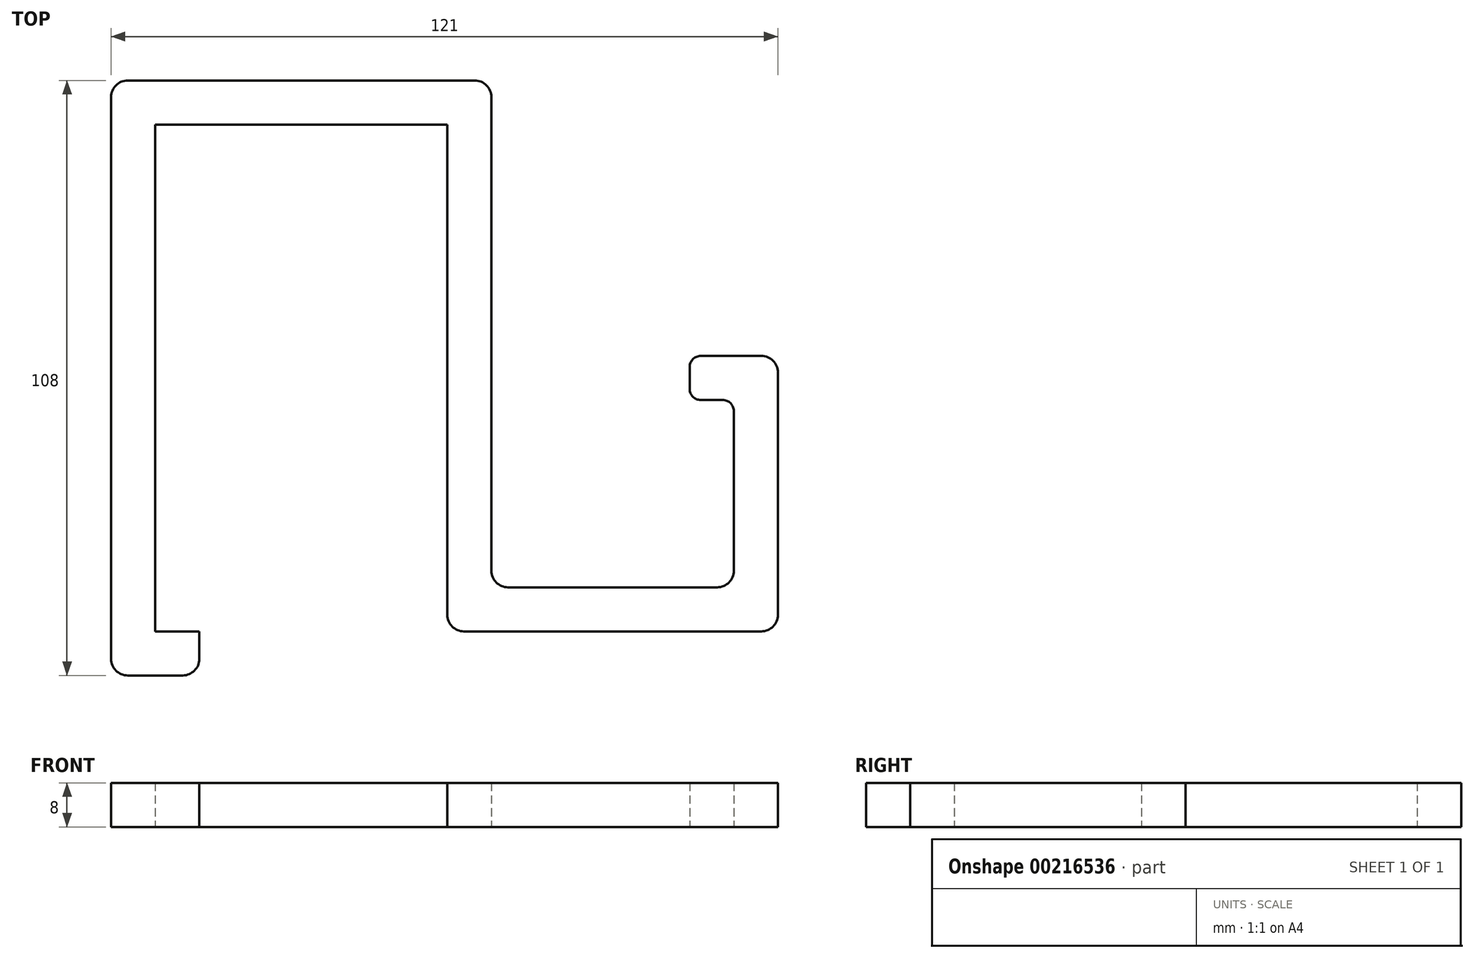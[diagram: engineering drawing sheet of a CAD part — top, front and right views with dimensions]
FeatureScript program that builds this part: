
annotation { "Feature Type Name" : "Feature", "Feature Type Description" : "" }
export const myFeature = defineFeature(function(context is Context, id is Id, definition is map)
    precondition{}
    {
        {
            assignVariable(context, id + "F0", {"name" : "dik", "anyValue" : 8});
        }
        {
            var Q0;
            Q0=qCreatedBy(makeId("Top.planeOp"),FACE);
            var sketch = newSketch(context, id + "F1", { "sketchPlane" : qUnion([Q0])});
            skLineSegment(sketch, "E0", {"start": v(0, 0) * mm, "end": v(0, 92) * mm});
            skLineSegment(sketch, "E1", {"start": v(0, 92) * mm, "end": v(53, 92) * mm});
            skLineSegment(sketch, "E2", {"start": v(53, 92) * mm, "end": v(53, 3) * mm});
            skLineSegment(sketch, "E3", {"start": v(0, 0) * mm, "end": v(-8, 0) * mm, "construction": true});
            skLineSegment(sketch, "E4", {"start": v(-8, 0) * mm, "end": v(-8, 97) * mm});
            skLineSegment(sketch, "E5", {"start": v(-5, 100) * mm, "end": v(58, 100) * mm});
            skLineSegment(sketch, "E6", {"start": v(61, 97) * mm, "end": v(61, 11) * mm});
            skLineSegment(sketch, "E7", {"start": v(56, 0) * mm, "end": v(110, 0) * mm});
            skLineSegment(sketch, "E8", {"start": v(113, 3) * mm, "end": v(113, 47) * mm});
            skLineSegment(sketch, "E9", {"start": v(110, 50) * mm, "end": v(105, 50) * mm});
            skLineSegment(sketch, "E10", {"start": v(105, 40) * mm, "end": v(105, 11) * mm});
            skLineSegment(sketch, "E11", {"start": v(102, 8) * mm, "end": v(64, 8) * mm});
            skLineSegment(sketch, "E12", {"start": v(105, 50) * mm, "end": v(99, 50) * mm});
            skLineSegment(sketch, "E13", {"start": v(97, 48) * mm, "end": v(97, 44) * mm});
            skLineSegment(sketch, "E14", {"start": v(99, 42) * mm, "end": v(103, 42) * mm});
            skLineSegment(sketch, "E15", {"start": v(-8, 0) * mm, "end": v(-8, -5) * mm});
            skLineSegment(sketch, "E16", {"start": v(-5, -8) * mm, "end": v(5, -8) * mm});
            skLineSegment(sketch, "E17", {"start": v(8, -5) * mm, "end": v(8, 0) * mm});
            skLineSegment(sketch, "E18", {"start": v(8, 0) * mm, "end": v(0, 0) * mm});
            skPoint(sketch, "E19.visualSharp", {"position": v(-8, 100) * mm});
            skArc(sketch, "E19.filletArc", {"start": v(-5, 100) * mm, "mid": v(-7.12, 99.12) * mm, "end": v(-8, 97) * mm});
            skPoint(sketch, "E20.visualSharp", {"position": v(61, 100) * mm});
            skArc(sketch, "E20.filletArc", {"start": v(61, 97) * mm, "mid": v(60.12, 99.12) * mm, "end": v(58, 100) * mm});
            skPoint(sketch, "E21.newPointA", {"position": v(105, 42) * mm});
            skArc(sketch, "E21.filletArc", {"start": v(105, 40) * mm, "mid": v(104.41, 41.41) * mm, "end": v(103, 42) * mm});
            skPoint(sketch, "E22.visualSharp", {"position": v(113, 50) * mm});
            skArc(sketch, "E22.filletArc", {"start": v(113, 47) * mm, "mid": v(112.12, 49.12) * mm, "end": v(110, 50) * mm});
            skPoint(sketch, "E23.visualSharp", {"position": v(113, 0) * mm});
            skArc(sketch, "E23.filletArc", {"start": v(110, 0) * mm, "mid": v(112.12, 0.88) * mm, "end": v(113, 3) * mm});
            skPoint(sketch, "E24.visualSharp", {"position": v(105, 8) * mm});
            skArc(sketch, "E24.filletArc", {"start": v(102, 8) * mm, "mid": v(104.12, 8.88) * mm, "end": v(105, 11) * mm});
            skPoint(sketch, "E25.newPointA", {"position": v(61, 8) * mm});
            skPoint(sketch, "E25.newPointB", {"position": v(61, 0) * mm});
            skArc(sketch, "E25.filletArc", {"start": v(61, 11) * mm, "mid": v(61.88, 8.88) * mm, "end": v(64, 8) * mm});
            skPoint(sketch, "E26.visualSharp", {"position": v(53, 0) * mm});
            skArc(sketch, "E26.filletArc", {"start": v(53, 3) * mm, "mid": v(53.88, 0.88) * mm, "end": v(56, 0) * mm});
            skPoint(sketch, "E27.visualSharp", {"position": v(-8, -8) * mm});
            skArc(sketch, "E27.filletArc", {"start": v(-8, -5) * mm, "mid": v(-7.12, -7.12) * mm, "end": v(-5, -8) * mm});
            skPoint(sketch, "E28.visualSharp", {"position": v(8, -8) * mm});
            skArc(sketch, "E28.filletArc", {"start": v(5, -8) * mm, "mid": v(7.12, -7.12) * mm, "end": v(8, -5) * mm});
            skPoint(sketch, "E29.visualSharp", {"position": v(97, 42) * mm});
            skArc(sketch, "E29.filletArc", {"start": v(97, 44) * mm, "mid": v(97.59, 42.59) * mm, "end": v(99, 42) * mm});
            skPoint(sketch, "E30.visualSharp", {"position": v(97, 50) * mm});
            skArc(sketch, "E30.filletArc", {"start": v(99, 50) * mm, "mid": v(97.59, 49.41) * mm, "end": v(97, 48) * mm});
            skSolve(sketch);
        }
        {
            var Q0;
            Q0=makeQuery(id+"F1.imprint","IMPRINT",FACE,{"disambiguationData":[TD([[makeQuery(id+"F1.imprint","IMPRINT",EDGE,{"derivedFrom":sQuery(id+"F1.wireOp",EDGE,"E0")}),1.0]])]});
            extrude(context, id + "F2", {"entities" : qUnion([Q0]), "depth" : (getVariable(context, 'dik')) * mm});
        }
    });
